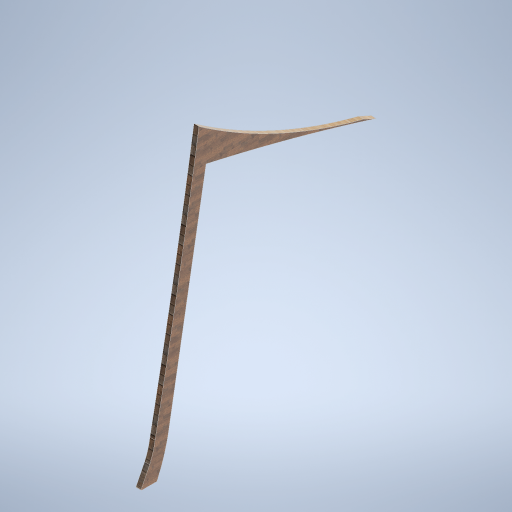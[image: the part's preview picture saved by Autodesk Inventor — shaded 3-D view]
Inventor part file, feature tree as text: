
AUTODESK INVENTOR PART (.ipt)
format: ipt  version: 2024.2 (Build 282272000, 272)  size: 311,296 bytes
history: native  units: mm
features: extrude x1, fillet x1, sketch x1
ambient origin geometry x8: Origin, YZ Plane, XZ Plane, XY Plane, X Axis, Y Axis, Z Axis, Center Point
bodies: Body1 (feature_tree)
feature tree (3):
  extrude  "Extrusion2"  Depth=10.0mm
  fillet  "Fillet1"  [1 undecoded]
  sketch  "Sketch1"  dims[d0=5000.0mm d1=29.670597mm d4=75.0deg d9=120000.0mm d11=100.0mm d12=0.0mm d13=40000.0mm d14=10.0mm]
note: 1 required parameter value undecoded (feature->parameter linkage not recoverable at this tier; creation-order binding heuristic only, values carry confidence <= 0.55)
